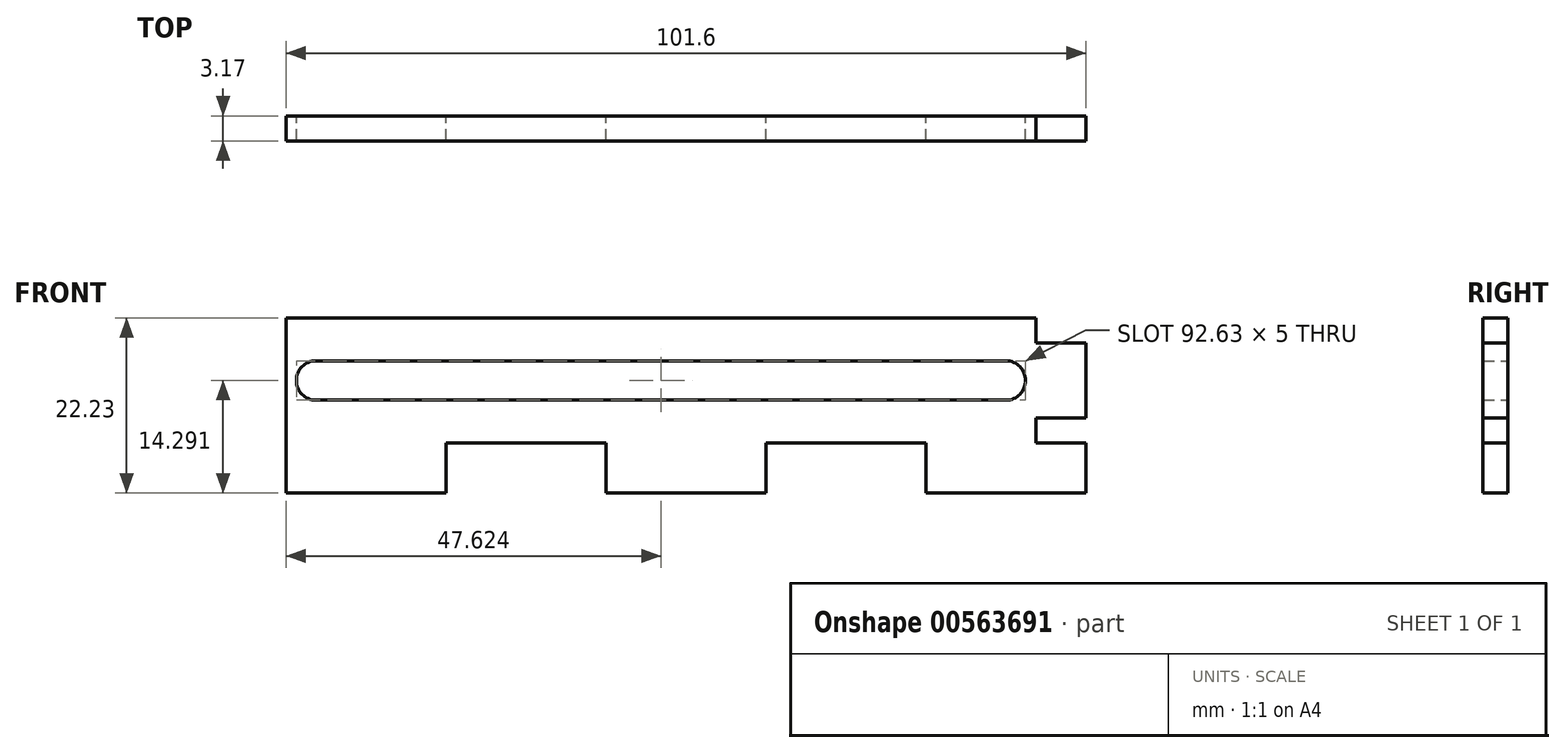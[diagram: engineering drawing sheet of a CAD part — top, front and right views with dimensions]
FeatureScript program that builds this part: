
annotation { "Feature Type Name" : "Feature", "Feature Type Description" : "" }
export const myFeature = defineFeature(function(context is Context, id is Id, definition is map)
    precondition{}
    {
        {
            var Q0;
            Q0=qCreatedBy(makeId("Front.planeOp"),FACE);
            var sketch = newSketch(context, id + "F0", { "sketchPlane" : qUnion([Q0])});
            skLineSegment(sketch, "E0", {"start": v(-25.84, -31.58) * mm, "end": v(-46.16, -31.58) * mm});
            skLineSegment(sketch, "E1", {"start": v(-46.16, -31.58) * mm, "end": v(-46.16, -25.23) * mm});
            skLineSegment(sketch, "E2", {"start": v(-46.16, -25.23) * mm, "end": v(-66.48, -25.23) * mm});
            skLineSegment(sketch, "E3", {"start": v(-66.48, -25.23) * mm, "end": v(-66.48, -31.58) * mm});
            skLineSegment(sketch, "E4", {"start": v(-66.48, -31.58) * mm, "end": v(-86.8, -31.58) * mm});
            skLineSegment(sketch, "E5", {"start": v(-86.8, -31.58) * mm, "end": v(-86.8, -25.23) * mm});
            skLineSegment(sketch, "E6", {"start": v(-86.8, -25.23) * mm, "end": v(-107.12, -25.23) * mm});
            skLineSegment(sketch, "E7", {"start": v(-107.12, -25.23) * mm, "end": v(-107.12, -31.58) * mm});
            skLineSegment(sketch, "E8", {"start": v(-107.12, -31.58) * mm, "end": v(-127.44, -31.58) * mm});
            skLineSegment(sketch, "E9", {"start": v(-127.44, -31.58) * mm, "end": v(-127.44, -9.35) * mm});
            skLineSegment(sketch, "E10", {"start": v(-123.63, -14.79) * mm, "end": v(-36, -14.79) * mm});
            skArc(sketch, "E11", {"start": v(-123.63, -14.79) * mm, "mid": v(-126.13, -17.29) * mm, "end": v(-123.63, -19.79) * mm});
            skArc(sketch, "E12", {"start": v(-36, -14.79) * mm, "mid": v(-33.5, -17.29) * mm, "end": v(-36, -19.79) * mm});
            skLineSegment(sketch, "E13", {"start": v(-123.63, -19.79) * mm, "end": v(-36, -19.79) * mm});
            skLineSegment(sketch, "E14", {"start": v(-32.2, -9.35) * mm, "end": v(-32.2, -12.53) * mm});
            skLineSegment(sketch, "E15", {"start": v(-32.2, -12.53) * mm, "end": v(-25.84, -12.53) * mm});
            skLineSegment(sketch, "E16", {"start": v(-25.84, -12.53) * mm, "end": v(-25.84, -22.05) * mm});
            skLineSegment(sketch, "E17", {"start": v(-25.84, -22.05) * mm, "end": v(-32.2, -22.05) * mm});
            skLineSegment(sketch, "E18", {"start": v(-32.2, -22.05) * mm, "end": v(-32.2, -25.23) * mm});
            skLineSegment(sketch, "E19", {"start": v(-32.2, -25.23) * mm, "end": v(-25.84, -25.23) * mm});
            skLineSegment(sketch, "E20", {"start": v(-25.84, -25.23) * mm, "end": v(-25.84, -31.58) * mm});
            skLineSegment(sketch, "E21", {"start": v(-32.2, -9.35) * mm, "end": v(-127.44, -9.35) * mm});
            skSolve(sketch);
        }
        {
            var Q0;
            Q0=makeQuery(id+"F0.imprint","IMPRINT",FACE,{"disambiguationData":[TD([[makeQuery(id+"F0.imprint","IMPRINT",EDGE,{"derivedFrom":sQuery(id+"F0.wireOp",EDGE,"E0")}),-1.0]])]});
            extrude(context, id + "F1", {"entities" : qUnion([Q0]), "depth" : 3.17 * mm, "offsetDistance" : 25.4 * mm});
        }
    });
